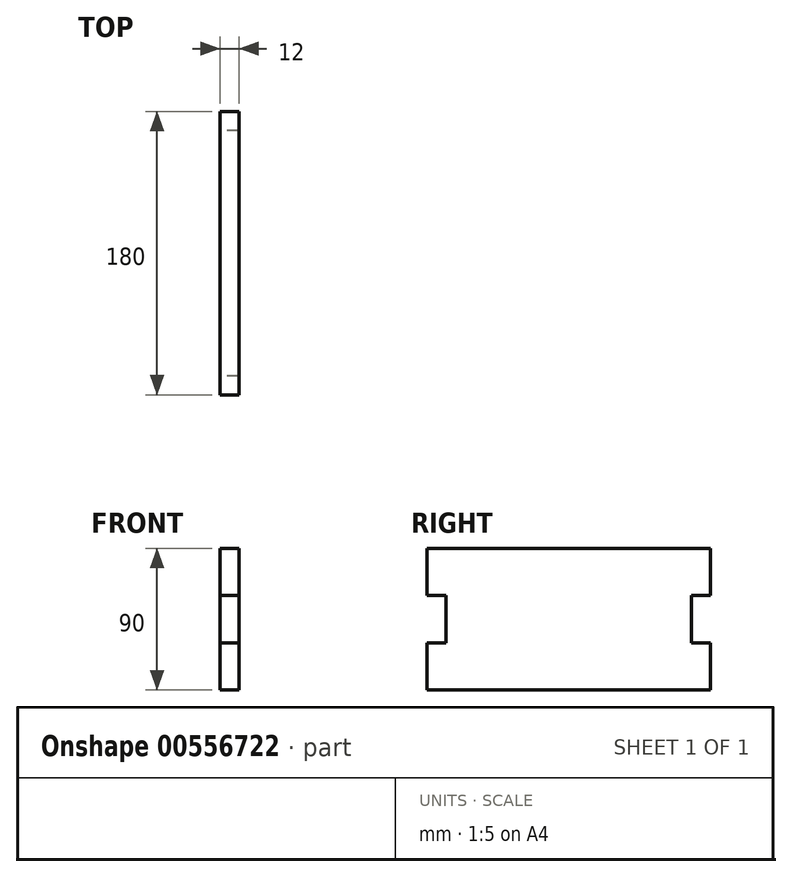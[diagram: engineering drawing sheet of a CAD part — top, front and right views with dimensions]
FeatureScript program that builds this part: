
annotation { "Feature Type Name" : "Feature", "Feature Type Description" : "" }
export const myFeature = defineFeature(function(context is Context, id is Id, definition is map)
    precondition{}
    {
        {
            var Q0;
            Q0=qCreatedBy(makeId("Right.planeOp"),FACE);
            var sketch = newSketch(context, id + "F0", { "sketchPlane" : qUnion([Q0])});
            skLineSegment(sketch, "E0", {"start": v(0, 0) * mm, "end": v(0, 30) * mm});
            skLineSegment(sketch, "E1", {"start": v(0, 30) * mm, "end": v(12, 30) * mm});
            skLineSegment(sketch, "E2", {"start": v(12, 30) * mm, "end": v(12, 60) * mm});
            skLineSegment(sketch, "E3", {"start": v(12, 60) * mm, "end": v(0, 60) * mm});
            skLineSegment(sketch, "E4", {"start": v(0, 60) * mm, "end": v(0, 90) * mm});
            skLineSegment(sketch, "E5", {"start": v(0, 90) * mm, "end": v(90, 90) * mm});
            skLineSegment(sketch, "E6", {"start": v(90, 90) * mm, "end": v(90, 0) * mm, "construction": true});
            skLineSegment(sketch, "E7", {"start": v(0, 0) * mm, "end": v(90, 0) * mm});
            skLineSegment(sketch, "E8.MirrorCS", {"start": v(168, 60) * mm, "end": v(180, 60) * mm});
            skLineSegment(sketch, "E9.MirrorCS", {"start": v(180, 0) * mm, "end": v(180, 30) * mm});
            skLineSegment(sketch, "E10.MirrorCS", {"start": v(180, 30) * mm, "end": v(168, 30) * mm});
            skLineSegment(sketch, "E11.MirrorCS", {"start": v(168, 30) * mm, "end": v(168, 60) * mm});
            skLineSegment(sketch, "E12.MirrorCS", {"start": v(180, 60) * mm, "end": v(180, 90) * mm});
            skLineSegment(sketch, "E13.MirrorCS", {"start": v(180, 0) * mm, "end": v(90, 0) * mm});
            skLineSegment(sketch, "E14.MirrorCS", {"start": v(180, 90) * mm, "end": v(90, 90) * mm});
            skSolve(sketch);
        }
        {
            var Q0;
            Q0 = qSketchRegion(id + "F0", true);
            extrude(context, id + "F1", {"entities" : qUnion([Q0]), "endBound" : BoundingType.SYMMETRIC, "depth" : 12 * mm, "offsetDistance" : 25 * mm});
        }
    });
